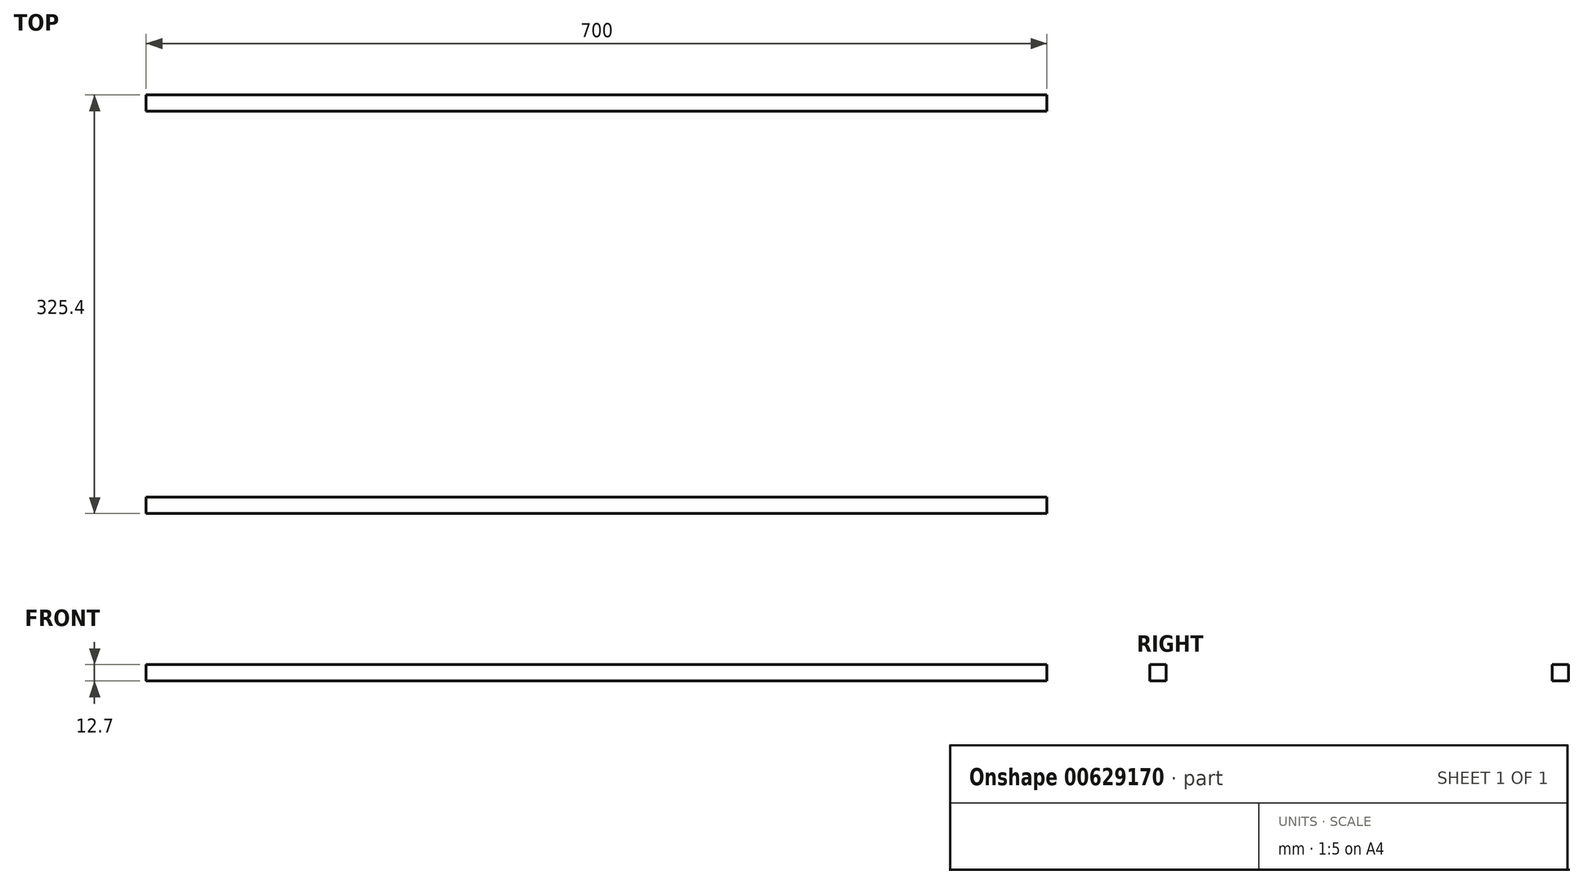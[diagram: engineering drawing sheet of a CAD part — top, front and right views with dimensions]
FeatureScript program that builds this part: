
annotation { "Feature Type Name" : "Feature", "Feature Type Description" : "" }
export const myFeature = defineFeature(function(context is Context, id is Id, definition is map)
    precondition{}
    {
        {
            var Q0;
            Q0=qCreatedBy(makeId("Top.planeOp"),FACE);
            var sketch = newSketch(context, id + "F0", { "sketchPlane" : qUnion([Q0])});
            skLineSegment(sketch, "E0.bottom", {"start": v(-365.44, -88.28) * mm, "end": v(334.56, -88.28) * mm});
            skLineSegment(sketch, "E0.top", {"start": v(-365.44, -100.98) * mm, "end": v(334.56, -100.98) * mm});
            skLineSegment(sketch, "E0.left", {"start": v(-365.44, -88.28) * mm, "end": v(-365.44, -100.98) * mm});
            skLineSegment(sketch, "E0.right", {"start": v(334.56, -88.28) * mm, "end": v(334.56, -100.98) * mm});
            skLineSegment(sketch, "E1.bottom", {"start": v(-365.44, -88.28) * mm, "end": v(-352.74, -88.28) * mm});
            skLineSegment(sketch, "E1.top", {"start": v(-365.44, 211.72) * mm, "end": v(-352.74, 211.72) * mm});
            skLineSegment(sketch, "E1.left", {"start": v(-365.44, -88.28) * mm, "end": v(-365.44, 211.72) * mm});
            skLineSegment(sketch, "E1.right", {"start": v(-352.74, -88.28) * mm, "end": v(-352.74, 211.72) * mm});
            skLineSegment(sketch, "E2.bottom", {"start": v(-365.44, 211.72) * mm, "end": v(334.56, 211.72) * mm});
            skLineSegment(sketch, "E2.top", {"start": v(-365.44, 224.42) * mm, "end": v(334.56, 224.42) * mm});
            skLineSegment(sketch, "E2.left", {"start": v(-365.44, 211.72) * mm, "end": v(-365.44, 224.42) * mm});
            skLineSegment(sketch, "E2.right", {"start": v(334.56, 211.72) * mm, "end": v(334.56, 224.42) * mm});
            skLineSegment(sketch, "E3.bottom", {"start": v(334.56, 211.72) * mm, "end": v(321.86, 211.72) * mm});
            skLineSegment(sketch, "E3.top", {"start": v(334.56, -88.28) * mm, "end": v(321.86, -88.28) * mm});
            skLineSegment(sketch, "E3.left", {"start": v(334.56, 211.72) * mm, "end": v(334.56, -88.28) * mm});
            skLineSegment(sketch, "E3.right", {"start": v(321.86, 211.72) * mm, "end": v(321.86, -88.28) * mm});
            skSolve(sketch);
        }
        {
            var Q0;
            Q0=makeQuery(id+"F0.imprint","IMPRINT",FACE,{"disambiguationData":[TD([[makeQuery(id+"F0.imprint","IMPRINT",EDGE,{"derivedFrom":sQuery(id+"F0.wireOp",EDGE,"E2.top")}),-1.0]])]});
            var Q1;
            Q1=makeQuery(id+"F0.imprint","IMPRINT",FACE,{"disambiguationData":[TD([[makeQuery(id+"F0.imprint","IMPRINT",EDGE,{"derivedFrom":sQuery(id+"F0.wireOp",EDGE,"E3.bottom")}),1.0]])]});
            var Q2;
            Q2=makeQuery(id+"F0.imprint","IMPRINT",FACE,{"disambiguationData":[TD([[makeQuery(id+"F0.imprint","IMPRINT",EDGE,{"derivedFrom":sQuery(id+"F0.wireOp",EDGE,"E1.bottom")}),1.0]])]});
            var Q3;
            Q3=makeQuery(id+"F0.imprint","IMPRINT",FACE,{"disambiguationData":[TD([[makeQuery(id+"F0.imprint","IMPRINT",EDGE,{"derivedFrom":sQuery(id+"F0.wireOp",EDGE,"E0.bottom")}),-1.0]])]});
            extrude(context, id + "F1", {"entities" : qUnion([Q0, Q1, Q2, Q3]), "depth" : 12.7 * mm, "offsetDistance" : 25.4 * mm});
        }
    });
